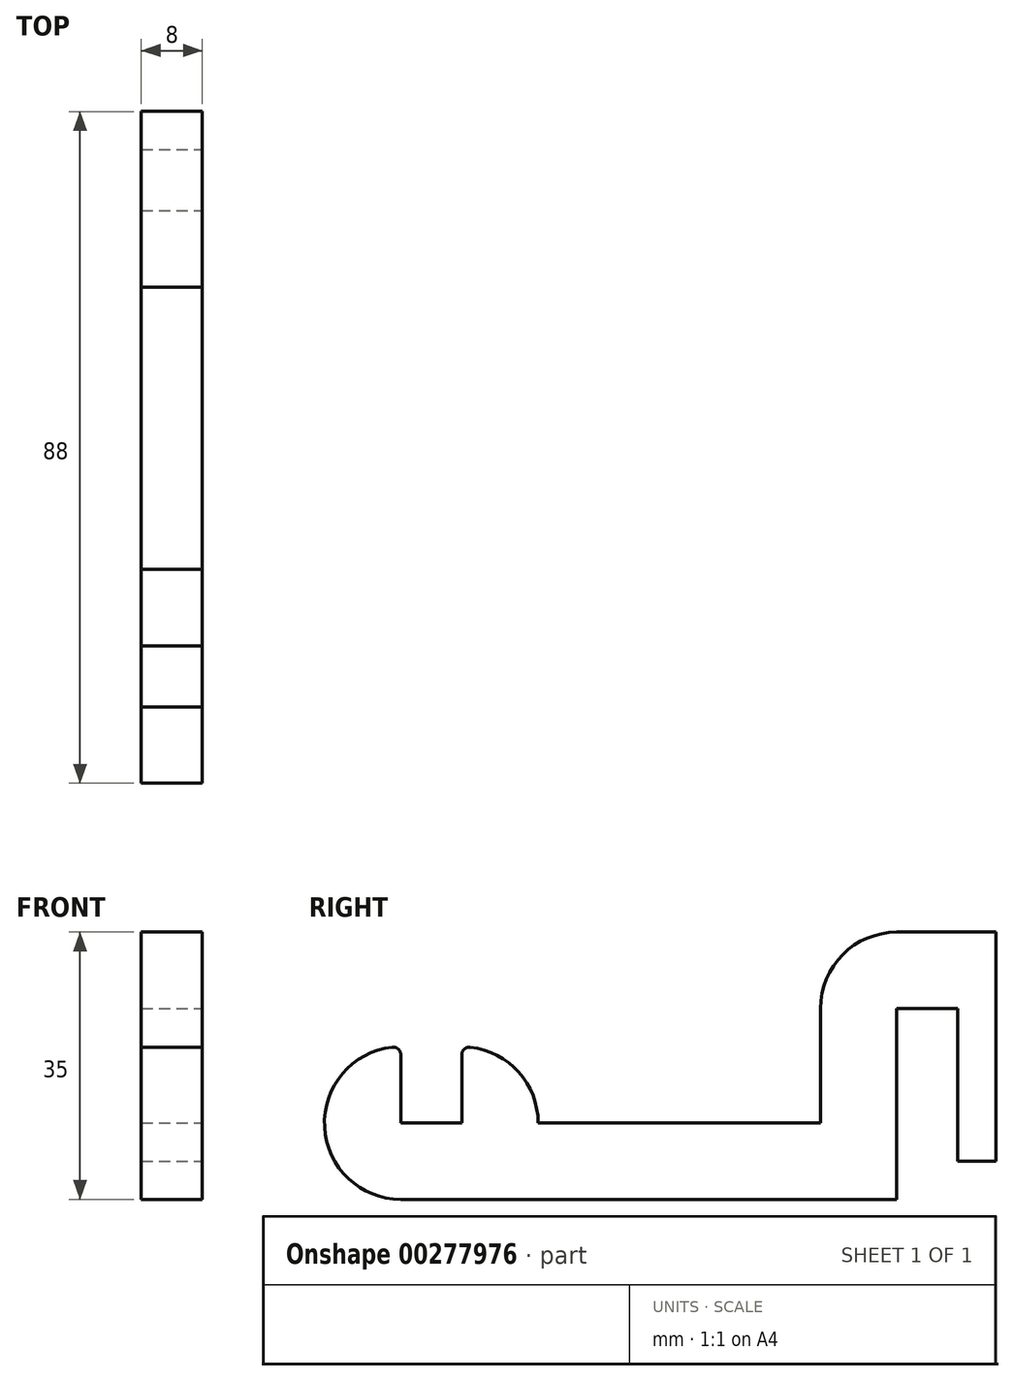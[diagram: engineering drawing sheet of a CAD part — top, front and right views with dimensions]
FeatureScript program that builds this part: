
annotation { "Feature Type Name" : "Feature", "Feature Type Description" : "" }
export const myFeature = defineFeature(function(context is Context, id is Id, definition is map)
    precondition{}
    {
        {
            var Q0;
            Q0=qCreatedBy(makeId("Right.planeOp"),FACE);
            var sketch = newSketch(context, id + "F0", { "sketchPlane" : qUnion([Q0])});
            skLineSegment(sketch, "E0", {"start": v(25.1, 227.52) * mm, "end": v(33.1, 227.52) * mm});
            skLineSegment(sketch, "E1", {"start": v(33.1, 227.52) * mm, "end": v(33.1, 207.52) * mm});
            skLineSegment(sketch, "E2", {"start": v(33.1, 207.52) * mm, "end": v(38.1, 207.52) * mm});
            skLineSegment(sketch, "E3", {"start": v(38.1, 207.52) * mm, "end": v(38.1, 237.52) * mm});
            skLineSegment(sketch, "E4", {"start": v(38.1, 237.52) * mm, "end": v(15.1, 237.52) * mm});
            skLineSegment(sketch, "E5", {"start": v(25.1, 227.52) * mm, "end": v(25.1, 202.52) * mm});
            skLineSegment(sketch, "E6", {"start": v(25.1, 202.52) * mm, "end": v(-49.9, 202.52) * mm});
            skLineSegment(sketch, "E7", {"start": v(-49.9, 202.52) * mm, "end": v(-49.9, 222.52) * mm});
            skLineSegment(sketch, "E8", {"start": v(-49.9, 222.52) * mm, "end": v(-39.9, 222.52) * mm});
            skLineSegment(sketch, "E9", {"start": v(-39.9, 222.52) * mm, "end": v(-39.9, 212.52) * mm});
            skLineSegment(sketch, "E10", {"start": v(-39.9, 212.52) * mm, "end": v(-31.9, 212.52) * mm});
            skLineSegment(sketch, "E11", {"start": v(-31.9, 212.52) * mm, "end": v(-31.9, 222.52) * mm});
            skLineSegment(sketch, "E12", {"start": v(-31.9, 222.52) * mm, "end": v(-21.9, 222.52) * mm});
            skLineSegment(sketch, "E13", {"start": v(-21.9, 222.52) * mm, "end": v(-21.9, 212.52) * mm});
            skLineSegment(sketch, "E14", {"start": v(15.1, 237.52) * mm, "end": v(15.1, 212.52) * mm});
            skLineSegment(sketch, "E15", {"start": v(15.1, 212.52) * mm, "end": v(-21.9, 212.52) * mm});
            skSolve(sketch);
        }
        {
            var Q0;
            Q0=qSketchRegion(id+"F0",true);
            extrude(context, id + "F1", {"entities" : qUnion([Q0]), "oppositeDirection" : true, "depth" : 8 * mm});
        }
        {
            var Q0;
            Q0=makeQuery(id+"F1.opExtrude","SWEPT_EDGE",EDGE,{"disambiguationData":[OSD([sQuery(id+"F0.wireOp",EDGE,"E4"),sQuery(id+"F0.wireOp",EDGE,"E14")])]});
            var Q1;
            Q1=makeQuery(id+"F1.opExtrude","SWEPT_EDGE",EDGE,{"disambiguationData":[OSD([sQuery(id+"F0.wireOp",EDGE,"E7"),sQuery(id+"F0.wireOp",EDGE,"E8")])]});
            var Q2;
            Q2=makeQuery(id+"F1.opExtrude","SWEPT_EDGE",EDGE,{"disambiguationData":[OSD([sQuery(id+"F0.wireOp",EDGE,"E6"),sQuery(id+"F0.wireOp",EDGE,"E7")])]});
            var Q3;
            Q3=makeQuery(id+"F1.opExtrude","SWEPT_EDGE",EDGE,{"disambiguationData":[OSD([sQuery(id+"F0.wireOp",EDGE,"E12"),sQuery(id+"F0.wireOp",EDGE,"E13")])]});
            fillet(context, id + "F2", {"entities" : qUnion([Q0, Q1, Q2, Q3]), "radius" : 10 * mm, "tangentPropagation" : true, "allowEdgeOverflow" : false});
        }
        {
            var Q0;
            Q0=makeQuery(id+"F2.opFillet","BLEND_EDGE",EDGE,{"blendedFrom":[makeQuery(id+"F1.opExtrude","SWEPT_EDGE",EDGE,{"disambiguationData":[OSD([sQuery(id+"F0.wireOp",EDGE,"E7"),sQuery(id+"F0.wireOp",EDGE,"E8")])]}),makeQuery(id+"F1.opExtrude","SWEPT_FACE",FACE,{"disambiguationData":[OSD([sQuery(id+"F0.wireOp",EDGE,"E9")])]})],"blendedInto":[makeQuery(id+"F1.opExtrude","SWEPT_FACE",FACE,{"disambiguationData":[OSD([sQuery(id+"F0.wireOp",EDGE,"E9")])]})]});
            var Q1;
            Q1=makeQuery(id+"F2.opFillet","BLEND_EDGE",EDGE,{"blendedFrom":[makeQuery(id+"F1.opExtrude","SWEPT_EDGE",EDGE,{"disambiguationData":[OSD([sQuery(id+"F0.wireOp",EDGE,"E12"),sQuery(id+"F0.wireOp",EDGE,"E13")])]}),makeQuery(id+"F1.opExtrude","SWEPT_FACE",FACE,{"disambiguationData":[OSD([sQuery(id+"F0.wireOp",EDGE,"E11")])]})],"blendedInto":[makeQuery(id+"F1.opExtrude","SWEPT_FACE",FACE,{"disambiguationData":[OSD([sQuery(id+"F0.wireOp",EDGE,"E11")])]})]});
            fillet(context, id + "F3", {"entities" : qUnion([Q0, Q1]), "radius" : 1 * mm, "tangentPropagation" : true, "allowEdgeOverflow" : false});
        }
    });
